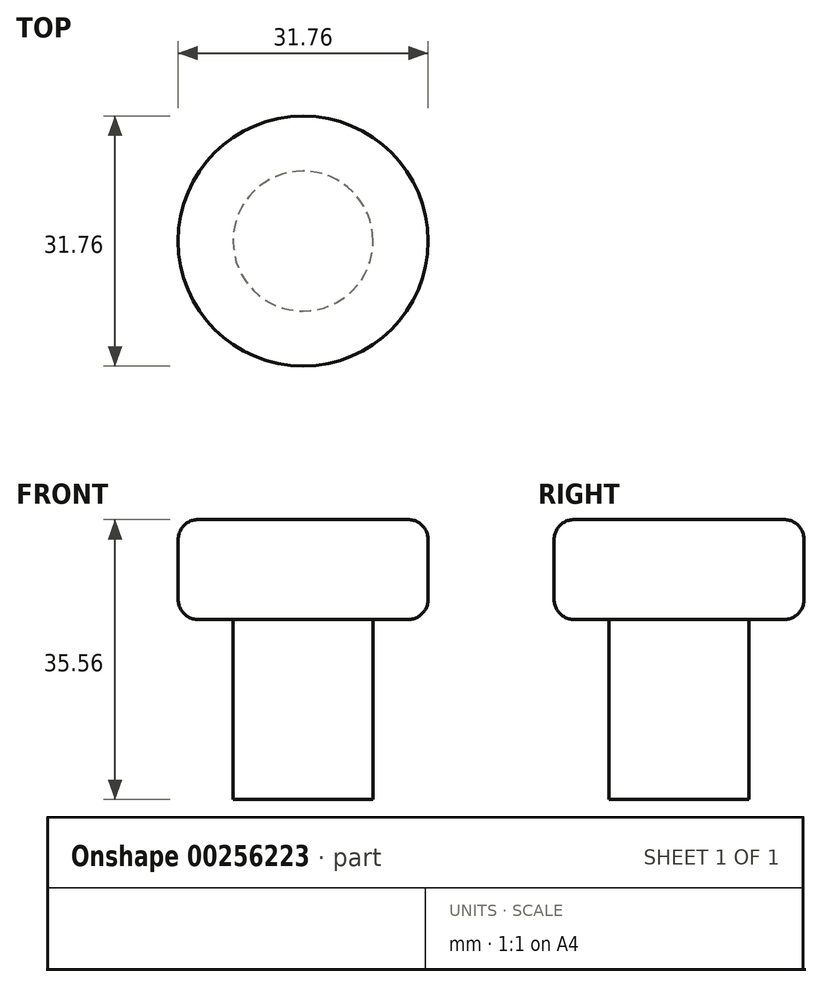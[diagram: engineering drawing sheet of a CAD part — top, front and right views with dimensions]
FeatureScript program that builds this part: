
annotation { "Feature Type Name" : "Feature", "Feature Type Description" : "" }
export const myFeature = defineFeature(function(context is Context, id is Id, definition is map)
    precondition{}
    {
        {
            var Q0;
            Q0=qCreatedBy(makeId("Top.planeOp"),FACE);
            var sketch = newSketch(context, id + "F0", { "sketchPlane" : qUnion([Q0])});
            skCircle(sketch, "E0", {"center": v(0, 0) * mm, "radius": 15.88 * mm});
            skSolve(sketch);
        }
        {
            var Q0;
            Q0=makeQuery(id+"F0.imprint","IMPRINT",FACE,{"disambiguationData":[TD([[makeQuery(id+"F0.imprint","IMPRINT",EDGE,{"derivedFrom":sQuery(id+"F0.wireOp",EDGE,"E0")}),1.0]])]});
            extrude(context, id + "F1", {"entities" : qUnion([Q0]), "depth" : 12.7 * mm});
        }
        {
            var Q0;
            Q0=makeQuery(id+"F1.opExtrude","CAP_EDGE",EDGE,{"disambiguationData":[OSD([sQuery(id+"F0.wireOp",EDGE,"E0")])],"isStart":false});
            var Q1;
            Q1=makeQuery(id+"F1.opExtrude","SWEPT_FACE",FACE,{"disambiguationData":[OSD([sQuery(id+"F0.wireOp",EDGE,"E0")])]});
            fillet(context, id + "F2", {"entities" : qUnion([Q0, Q1]), "radius" : 2.54 * mm, "tangentPropagation" : true, "allowEdgeOverflow" : false});
        }
        {
            var Q0;
            Q0=qCreatedBy(makeId("Top.planeOp"),FACE);
            var sketch = newSketch(context, id + "F3", { "sketchPlane" : qUnion([Q0])});
            skCircle(sketch, "E1", {"center": v(0, 0) * mm, "radius": 8.9 * mm});
            skSolve(sketch);
        }
        {
            var Q0;
            Q0=makeQuery(id+"F3.imprint","IMPRINT",FACE,{"disambiguationData":[TD([[makeQuery(id+"F3.imprint","IMPRINT",EDGE,{"derivedFrom":sQuery(id+"F3.wireOp",EDGE,"E1")}),1.0]])]});
            extrude(context, id + "F4", {"entities" : qUnion([Q0]), "operationType" : NewBodyOperationType.ADD, "oppositeDirection" : true, "depth" : 22.86 * mm});
        }
    });
